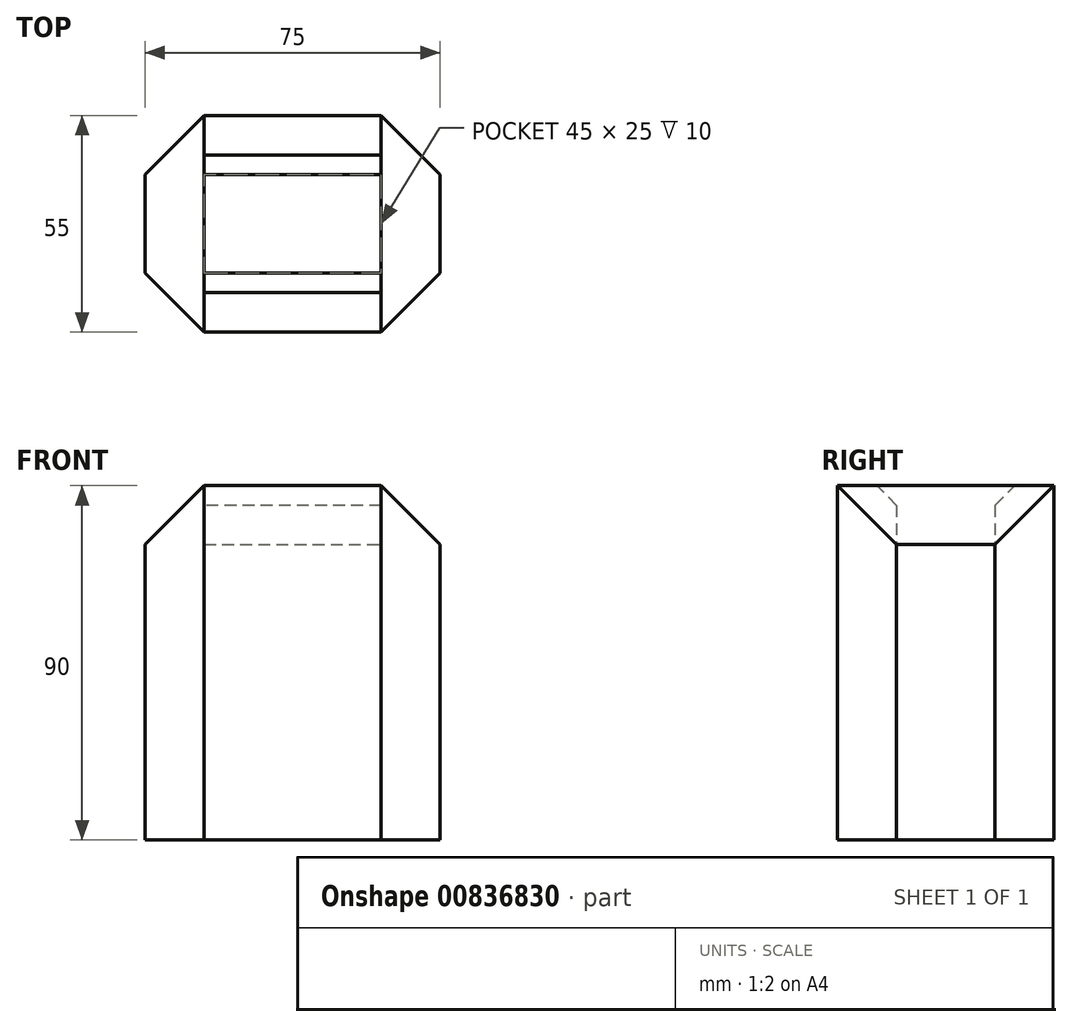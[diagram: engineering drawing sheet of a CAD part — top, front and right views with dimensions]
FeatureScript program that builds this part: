
annotation { "Feature Type Name" : "Feature", "Feature Type Description" : "" }
export const myFeature = defineFeature(function(context is Context, id is Id, definition is map)
    precondition{}
    {
        {
            var Q0;
            Q0=qCreatedBy(makeId("Top.planeOp"),FACE);
            var sketch = newSketch(context, id + "F0", { "sketchPlane" : qUnion([Q0])});
            skLineSegment(sketch, "E0.bottom", {"start": v(-22.5, 12.5) * mm, "end": v(22.5, 12.5) * mm});
            skLineSegment(sketch, "E0.top", {"start": v(-22.5, -12.5) * mm, "end": v(22.5, -12.5) * mm});
            skLineSegment(sketch, "E0.left", {"start": v(-22.5, 12.5) * mm, "end": v(-22.5, -12.5) * mm});
            skLineSegment(sketch, "E0.right", {"start": v(22.5, 12.5) * mm, "end": v(22.5, -12.5) * mm});
            skPoint(sketch, "E0.middle", {"position": v(0, 0) * mm});
            skLineSegment(sketch, "E1.bottom", {"start": v(-37.5, 27.5) * mm, "end": v(37.5, 27.5) * mm});
            skLineSegment(sketch, "E1.top", {"start": v(-37.5, -27.5) * mm, "end": v(37.5, -27.5) * mm});
            skLineSegment(sketch, "E1.left", {"start": v(-37.5, 27.5) * mm, "end": v(-37.5, -27.5) * mm});
            skLineSegment(sketch, "E1.right", {"start": v(37.5, 27.5) * mm, "end": v(37.5, -27.5) * mm});
            skLineSegment(sketch, "E2.top", {"start": v(-22.5, -27.5) * mm, "end": v(22.5, -27.5) * mm});
            skSolve(sketch);
        }
        {
            var Q0;
            Q0=makeQuery(id+"F0.imprint","IMPRINT",FACE,{"disambiguationData":[TD([[makeQuery(id+"F0.imprint","IMPRINT",EDGE,{"derivedFrom":sQuery(id+"F0.wireOp",EDGE,"E0.bottom")}),-1.0]])]});
            extrude(context, id + "F1", {"entities" : qUnion([Q0]), "depth" : 75 * mm, "offsetDistance" : 25 * mm});
        }
        {
            var Q0;
            Q0=makeQuery(id+"F0.imprint","IMPRINT",FACE,{"disambiguationData":[TD([[makeQuery(id+"F0.imprint","IMPRINT",EDGE,{"derivedFrom":sQuery(id+"F0.wireOp",EDGE,"E0.bottom")}),1.0]])]});
            extrude(context, id + "F2", {"entities" : qUnion([Q0]), "operationType" : NewBodyOperationType.ADD, "depth" : 90 * mm, "offsetDistance" : 25 * mm});
        }
        {
            var Q0;
            Q0=makeQuery(id+"F2.opExtrude","CAP_EDGE",EDGE,{"disambiguationData":[OSD([sQuery(id+"F0.wireOp",EDGE,"E1.left")])],"isStart":false});
            var Q1;
            Q1=makeQuery(id+"F2.opExtrude","CAP_EDGE",EDGE,{"disambiguationData":[OSD([sQuery(id+"F0.wireOp",EDGE,"E1.right")])],"isStart":false});
            var Q2;
            Q2=makeQuery(id+"F2.opExtrude","SWEPT_EDGE",EDGE,{"disambiguationData":[OSD([sQuery(id+"F0.wireOp",EDGE,"E1.bottom"),sQuery(id+"F0.wireOp",EDGE,"E1.right")])]});
            var Q3;
            Q3=makeQuery(id+"F2.opExtrude","SWEPT_EDGE",EDGE,{"disambiguationData":[OSD([sQuery(id+"F0.wireOp",EDGE,"E1.top"),sQuery(id+"F0.wireOp",EDGE,"E1.right")])]});
            var Q4;
            Q4=makeQuery(id+"F2.opExtrude","SWEPT_EDGE",EDGE,{"disambiguationData":[OSD([sQuery(id+"F0.wireOp",EDGE,"E1.top"),sQuery(id+"F0.wireOp",EDGE,"E1.left")])]});
            var Q5;
            Q5=makeQuery(id+"F2.opExtrude","SWEPT_EDGE",EDGE,{"disambiguationData":[OSD([sQuery(id+"F0.wireOp",EDGE,"E1.bottom"),sQuery(id+"F0.wireOp",EDGE,"E1.left")])]});
            chamfer(context, id + "F3", {"entities" : qUnion([Q0, Q1, Q2, Q3, Q4, Q5]), "width" : 15 * mm});
        }
        {
            var Q0;
            Q0=makeQuery(id+"F2.opExtrude","CAP_EDGE",EDGE,{"disambiguationData":[OSD([sQuery(id+"F0.wireOp",EDGE,"E0.bottom")])],"isStart":false});
            var Q1;
            Q1=makeQuery(id+"F2.opExtrude","CAP_EDGE",EDGE,{"disambiguationData":[OSD([sQuery(id+"F0.wireOp",EDGE,"E0.top")])],"isStart":false});
            chamfer(context, id + "F4", {"entities" : qUnion([Q0, Q1]), "width" : 5 * mm, "tangentPropagation" : true});
        }
    });
